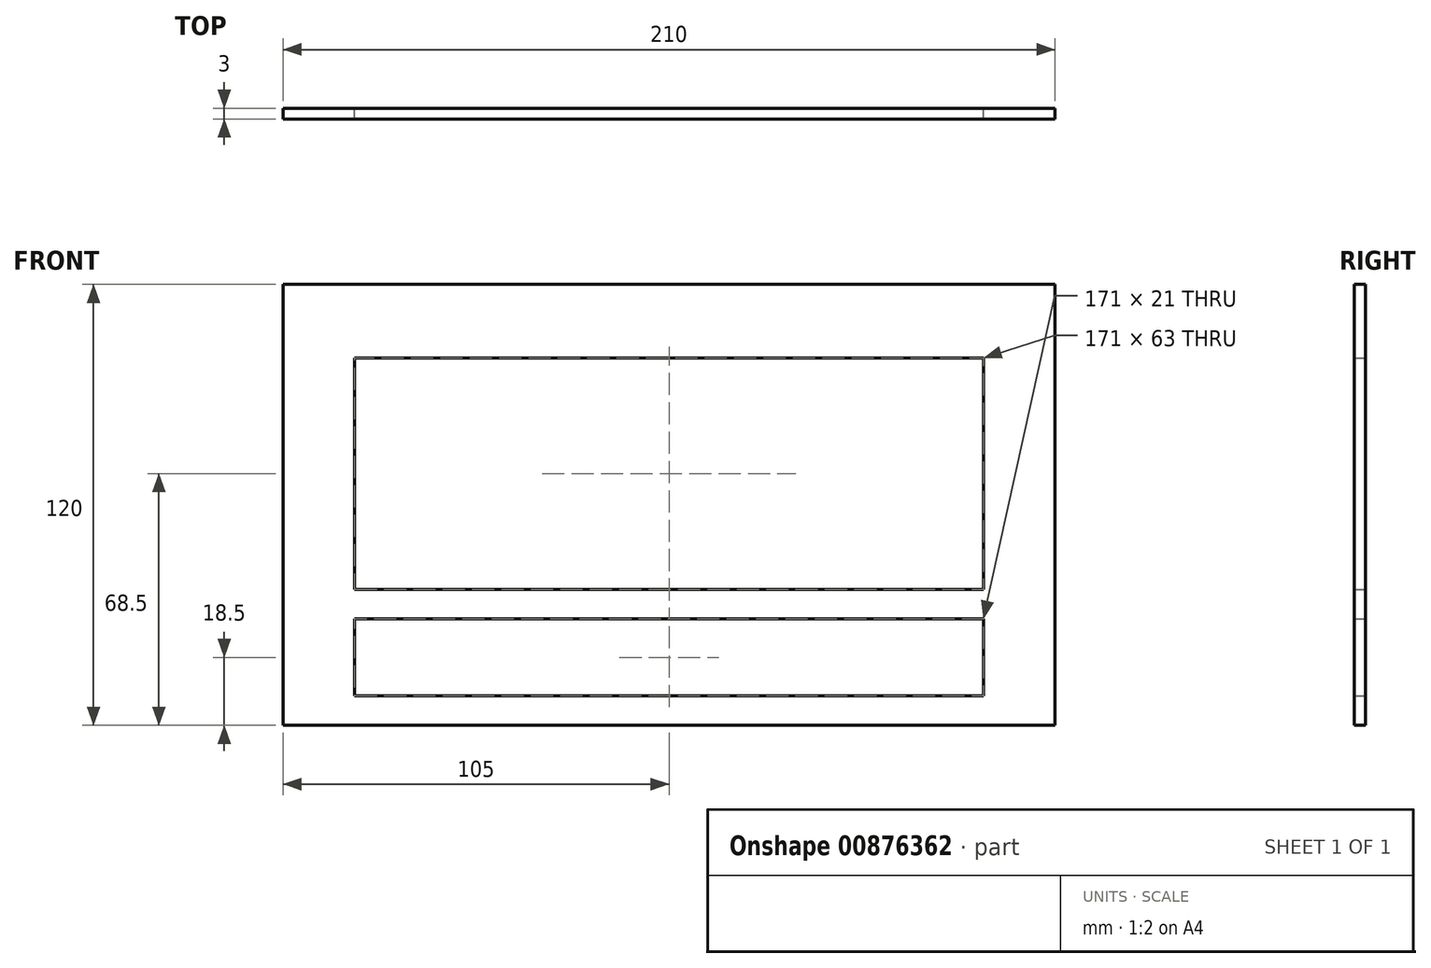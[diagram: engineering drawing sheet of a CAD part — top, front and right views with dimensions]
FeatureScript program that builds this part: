
annotation { "Feature Type Name" : "Feature", "Feature Type Description" : "" }
export const myFeature = defineFeature(function(context is Context, id is Id, definition is map)
    precondition{}
    {
        {
            var Q0;
            Q0=qCreatedBy(makeId("Front.planeOp"),FACE);
            var sketch = newSketch(context, id + "F0", { "sketchPlane" : qUnion([Q0])});
            skLineSegment(sketch, "E0.bottom", {"start": v(-105, 60) * mm, "end": v(105, 60) * mm});
            skLineSegment(sketch, "E0.top", {"start": v(-105, -60) * mm, "end": v(105, -60) * mm});
            skLineSegment(sketch, "E0.left", {"start": v(-105, 60) * mm, "end": v(-105, -60) * mm});
            skLineSegment(sketch, "E0.right", {"start": v(105, 60) * mm, "end": v(105, -60) * mm});
            skPoint(sketch, "E0.middle", {"position": v(0, 0) * mm});
            skLineSegment(sketch, "E1", {"start": v(0, 0) * mm, "end": v(0, 53.3) * mm, "construction": true});
            skLineSegment(sketch, "E2.bottom", {"start": v(-85.5, 40) * mm, "end": v(85.5, 40) * mm});
            skLineSegment(sketch, "E2.top", {"start": v(-85.5, -23) * mm, "end": v(85.5, -23) * mm});
            skLineSegment(sketch, "E2.left", {"start": v(-85.5, 40) * mm, "end": v(-85.5, -23) * mm});
            skLineSegment(sketch, "E2.right", {"start": v(85.5, 40) * mm, "end": v(85.5, -23) * mm});
            skPoint(sketch, "E2.middle", {"position": v(0, 8.5) * mm});
            skLineSegment(sketch, "E3.bottom", {"start": v(-85.5, -31) * mm, "end": v(85.5, -31) * mm});
            skLineSegment(sketch, "E3.top", {"start": v(-85.5, -52) * mm, "end": v(85.5, -52) * mm});
            skLineSegment(sketch, "E3.left", {"start": v(-85.5, -31) * mm, "end": v(-85.5, -52) * mm});
            skLineSegment(sketch, "E3.right", {"start": v(85.5, -31) * mm, "end": v(85.5, -52) * mm});
            skPoint(sketch, "E3.middle", {"position": v(0, -41.5) * mm});
            skSolve(sketch);
        }
        {
            var Q0;
            Q0 = qSketchRegion(id + "F0", true);
            extrude(context, id + "F1", {"entities" : qUnion([Q0]), "depth" : 3 * mm, "offsetDistance" : 25 * mm});
        }
    });
